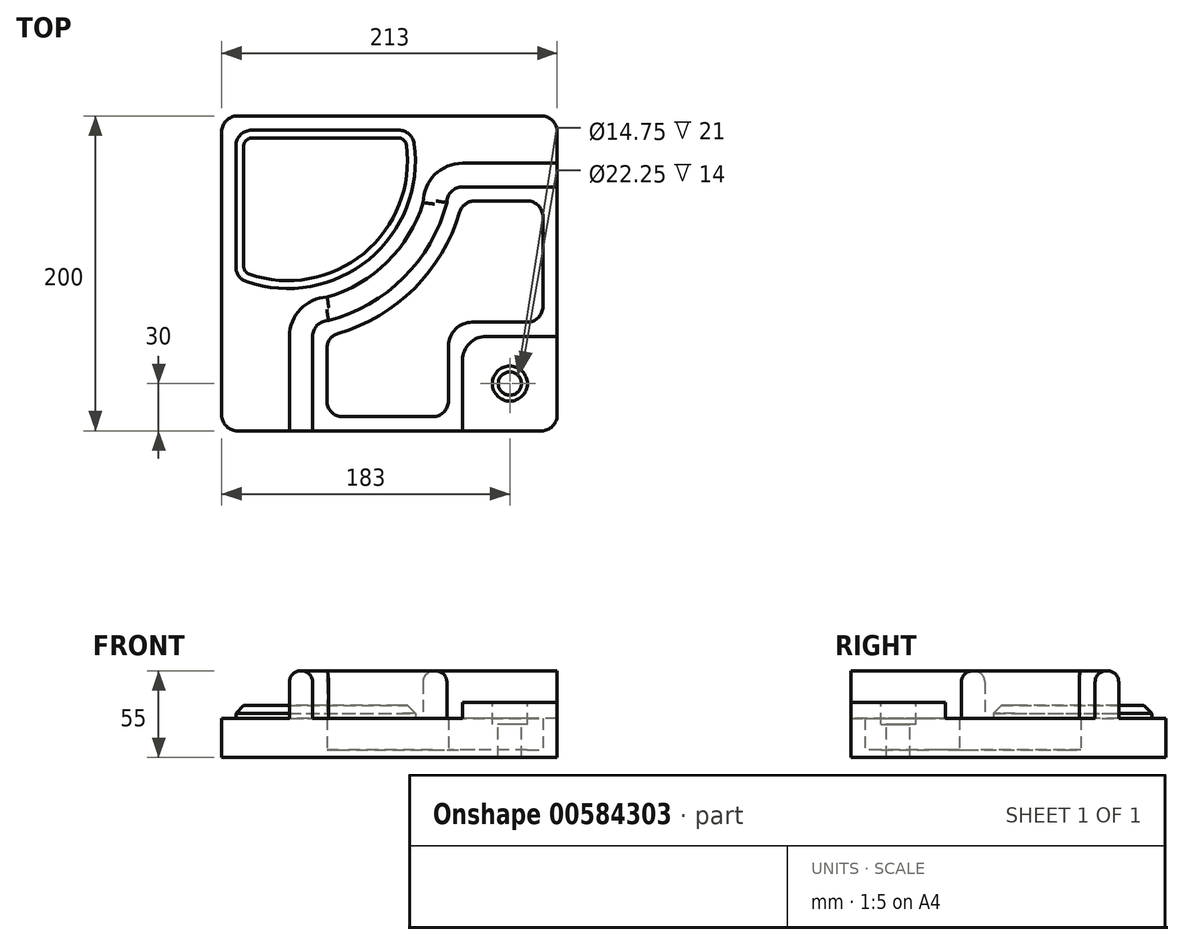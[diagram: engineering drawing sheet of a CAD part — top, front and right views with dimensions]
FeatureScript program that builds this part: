
annotation { "Feature Type Name" : "Feature", "Feature Type Description" : "" }
export const myFeature = defineFeature(function(context is Context, id is Id, definition is map)
    precondition{}
    {
        {
            var Q0;
            Q0=qCreatedBy(makeId("Top.planeOp"),FACE);
            var sketch = newSketch(context, id + "F0", { "sketchPlane" : qUnion([Q0])});
            skLineSegment(sketch, "E0", {"start": v(0, 0) * mm, "end": v(-106.5, 0) * mm});
            skLineSegment(sketch, "E1", {"start": v(-106.5, 0) * mm, "end": v(-106.5, 200) * mm});
            skLineSegment(sketch, "E2.MirrorCS", {"start": v(0, 0) * mm, "end": v(106.5, 0) * mm});
            skLineSegment(sketch, "E3.MirrorCS", {"start": v(106.5, 0) * mm, "end": v(106.5, 200) * mm});
            skLineSegment(sketch, "E4", {"start": v(-106.5, 200) * mm, "end": v(106.5, 200) * mm});
            skLineSegment(sketch, "E5", {"start": v(106.5, 60) * mm, "end": v(46.5, 60) * mm});
            skLineSegment(sketch, "E6", {"start": v(46.5, 60) * mm, "end": v(46.5, 0) * mm});
            skLineSegment(sketch, "E7", {"start": v(-63.5, 0) * mm, "end": v(-63.5, 60) * mm});
            skLineSegment(sketch, "E8", {"start": v(106.5, 170) * mm, "end": v(46.5, 170) * mm});
            skLineSegment(sketch, "E9", {"start": v(-48.73, 0) * mm, "end": v(-48.73, 60) * mm});
            skLineSegment(sketch, "E10", {"start": v(106.5, 155) * mm, "end": v(46.5, 155) * mm});
            skArc(sketch, "E11", {"start": v(-39.51, 84.98) * mm, "mid": v(-56.53, 77.32) * mm, "end": v(-63.5, 60) * mm});
            skArc(sketch, "E12", {"start": v(46.5, 170) * mm, "mid": v(28.82, 162.68) * mm, "end": v(21.5, 145) * mm});
            skArc(sketch, "E13", {"start": v(46.5, 155) * mm, "mid": v(39.43, 152.07) * mm, "end": v(36.5, 145) * mm});
            skArc(sketch, "E14", {"start": v(-38.73, 70) * mm, "mid": v(-45.8, 67.07) * mm, "end": v(-48.73, 60) * mm});
            skArc(sketch, "E15", {"start": v(-39.51, 84.98) * mm, "mid": v(-1.41, 107.27) * mm, "end": v(21.5, 145) * mm});
            skArc(sketch, "E16", {"start": v(-38.73, 70) * mm, "mid": v(9.07, 97.28) * mm, "end": v(36.5, 145) * mm});
            skLineSegment(sketch, "E17", {"start": v(97.5, 146) * mm, "end": v(97.5, 69) * mm});
            skLineSegment(sketch, "E18", {"start": v(97.5, 69) * mm, "end": v(37.5, 69) * mm});
            skLineSegment(sketch, "E19", {"start": v(37.5, 69) * mm, "end": v(37.5, 9) * mm});
            skLineSegment(sketch, "E20", {"start": v(37.5, 9) * mm, "end": v(-39.73, 9) * mm});
            skLineSegment(sketch, "E21", {"start": v(97.5, 146) * mm, "end": v(46.5, 146) * mm});
            skLineSegment(sketch, "E22", {"start": v(-39.73, 9) * mm, "end": v(-39.73, 60) * mm});
            skArc(sketch, "E23", {"start": v(-39.73, 60) * mm, "mid": v(15.83, 90.52) * mm, "end": v(46.5, 146) * mm});
            skArc(sketch, "E24", {"start": v(-97.5, 97.45) * mm, "mid": v(-12.49, 109.37) * mm, "end": v(14.07, 191) * mm});
            skLineSegment(sketch, "E25", {"start": v(0, 0) * mm, "end": v(0, 200) * mm, "construction": true});
            skLineSegment(sketch, "E26", {"start": v(-106.5, 100) * mm, "end": v(106.5, 100) * mm, "construction": true});
            skLineSegment(sketch, "E27", {"start": v(14.07, 191) * mm, "end": v(-97.5, 191) * mm});
            skLineSegment(sketch, "E28", {"start": v(-97.5, 97.45) * mm, "end": v(-97.5, 191) * mm});
            skSolve(sketch);
        }
        {
            var Q0;
            {var subQ1=sQuery(id+"F0.wireOp",EDGE,"E1");Q0=makeQuery(id+"F0.imprint","IMPRINT",FACE,{"disambiguationData":[TD([[makeQuery(id+"F0.imprint","IMPRINT",EDGE,{"derivedFrom":subQ1}),-1.0]])]});}
            var Q1;
            {var subQ6=sQuery(id+"F0.wireOp",EDGE,"E5");Q1=makeQuery(id+"F0.imprint","IMPRINT",FACE,{"disambiguationData":[TD([[makeQuery(id+"F0.imprint","IMPRINT",EDGE,{"derivedFrom":subQ6}),-1.0]])]});}
            extrude(context, id + "F1", {"entities" : qUnion([Q0, Q1]), "depth" : 25 * mm, "offsetDistance" : 25 * mm});
        }
        {
            var Q0;
            Q0=makeQuery(id+"F0.imprint","IMPRINT",FACE,{"disambiguationData":[TD([[makeQuery(id+"F0.imprint","IMPRINT",EDGE,{"derivedFrom":sQuery(id+"F0.wireOp",EDGE,"E24")}),1.0]])]});
            extrude(context, id + "F2", {"entities" : qUnion([Q0]), "operationType" : NewBodyOperationType.ADD, "depth" : 33 * mm, "offsetDistance" : 25 * mm});
        }
        {
            var Q0;
            Q0=makeQuery(id+"F0.imprint","IMPRINT",FACE,{"disambiguationData":[TD([[makeQuery(id+"F0.imprint","IMPRINT",EDGE,{"derivedFrom":sQuery(id+"F0.wireOp",EDGE,"E17")}),-1.0]])]});
            extrude(context, id + "F3", {"entities" : qUnion([Q0]), "operationType" : NewBodyOperationType.ADD, "depth" : 5 * mm, "offsetDistance" : 25 * mm});
        }
        {
            var Q0;
            {var subQ4=sQuery(id+"F0.wireOp",EDGE,"E5");Q0=makeQuery(id+"F0.imprint","IMPRINT",FACE,{"disambiguationData":[TD([[makeQuery(id+"F0.imprint","IMPRINT",EDGE,{"derivedFrom":subQ4}),1.0]])]});}
            extrude(context, id + "F4", {"entities" : qUnion([Q0]), "operationType" : NewBodyOperationType.ADD, "depth" : 35 * mm, "offsetDistance" : 25 * mm});
        }
        {
            var Q0;
            Q0=makeQuery(id+"F4.opExtrude","CAP_FACE",FACE,{"disambiguationData":[OSD([sQuery(id+"F0.wireOp",EDGE,"E2.MirrorCS"),sQuery(id+"F0.wireOp",EDGE,"E3.MirrorCS"),sQuery(id+"F0.wireOp",EDGE,"E5"),sQuery(id+"F0.wireOp",EDGE,"E6")])],"isStart":false});
            var sketch = newSketch(context, id + "F5", { "sketchPlane" : qUnion([Q0])});
            skLineSegment(sketch, "E29", {"start": v(76.5, 60) * mm, "end": v(76.5, 0) * mm, "construction": true});
            skLineSegment(sketch, "E30", {"start": v(46.5, 30) * mm, "end": v(106.5, 30) * mm, "construction": true});
            skPoint(sketch, "E31", {"position": v(76.5, 30) * mm});
            skSolve(sketch);
        }
        {
            var Q0;
            Q0=sQuery(id+"F5.wireOp",VERTEX,"E31");
            var Q1;
            Q1=makeQuery(id+"F1.opExtrude","SWEPT_BODY",BODY,{"disambiguationData":[OSD([sQuery(id+"F0.wireOp",EDGE,"E0"),sQuery(id+"F0.wireOp",EDGE,"E2.MirrorCS"),sQuery(id+"F0.wireOp",EDGE,"E3.MirrorCS"),sQuery(id+"F0.wireOp",EDGE,"E5"),sQuery(id+"F0.wireOp",EDGE,"E6"),sQuery(id+"F0.wireOp",EDGE,"E9"),sQuery(id+"F0.wireOp",EDGE,"E10"),sQuery(id+"F0.wireOp",EDGE,"E13"),sQuery(id+"F0.wireOp",EDGE,"E14"),sQuery(id+"F0.wireOp",EDGE,"E16"),sQuery(id+"F0.wireOp",EDGE,"E17"),sQuery(id+"F0.wireOp",EDGE,"E18"),sQuery(id+"F0.wireOp",EDGE,"E19"),sQuery(id+"F0.wireOp",EDGE,"E20"),sQuery(id+"F0.wireOp",EDGE,"E21"),sQuery(id+"F0.wireOp",EDGE,"E22"),sQuery(id+"F0.wireOp",EDGE,"E23")])]});
            hole(context, id + "F6", {"style" : HoleStyle.C_BORE, "endStyle" : HoleEndStyle.THROUGH, "standardTappedOrClearance" : lookupTablePath({ "standard" : "ISO", "fit" : "Close", "size" : "M14", "type" : "Clearance" }), "standardBlindInLast" : lookupTablePath({ "fit" : "Close", "standard" : "ISO", "size" : "M14", "type" : "Clearance" }), "holeDiameter" : 14.75 * mm, "cBoreDiameter" : 22.25 * mm, "cBoreDepth" : 14 * mm, "majorDiameter" : 5 * mm, "isTappedThrough" : true, "tappedDepth" : 12 * mm, "tapClearance" : 3, "locations" : qUnion([Q0]), "scope" : qUnion([Q1])});
        }
        {
            var Q0;
            {var subQ2=sQuery(id+"F0.wireOp",EDGE,"E7");Q0=makeQuery(id+"F0.imprint","IMPRINT",FACE,{"disambiguationData":[TD([[makeQuery(id+"F0.imprint","IMPRINT",EDGE,{"derivedFrom":subQ2}),-1.0]])]});}
            extrude(context, id + "F7", {"entities" : qUnion([Q0]), "operationType" : NewBodyOperationType.ADD, "depth" : 55 * mm, "offsetDistance" : 25 * mm});
        }
        {
            var Q0;
            Q0=makeQuery(id+"F4.opExtrude","SWEPT_EDGE",EDGE,{"disambiguationData":[OSD([sQuery(id+"F0.wireOp",EDGE,"E2.MirrorCS"),sQuery(id+"F0.wireOp",EDGE,"E3.MirrorCS")])]});
            var Q1;
            Q1=makeQuery(id+"F1.opExtrude","SWEPT_EDGE",EDGE,{"disambiguationData":[OSD([sQuery(id+"F0.wireOp",EDGE,"E0"),sQuery(id+"F0.wireOp",EDGE,"E1")])]});
            var Q2;
            Q2=makeQuery(id+"F1.opExtrude","SWEPT_EDGE",EDGE,{"disambiguationData":[OSD([sQuery(id+"F0.wireOp",EDGE,"E1"),sQuery(id+"F0.wireOp",EDGE,"E4")])]});
            var Q3;
            Q3=makeQuery(id+"F1.opExtrude","SWEPT_EDGE",EDGE,{"disambiguationData":[OSD([sQuery(id+"F0.wireOp",EDGE,"E3.MirrorCS"),sQuery(id+"F0.wireOp",EDGE,"E4")])]});
            fillet(context, id + "F8", {"entities" : qUnion([Q0, Q1, Q2, Q3]), "radius" : 10 * mm, "tangentPropagation" : true, "allowEdgeOverflow" : false});
        }
        {
            var Q0;
            Q0=makeQuery(id+"F1.opExtrude","SWEPT_EDGE",EDGE,{"disambiguationData":[OSD([sQuery(id+"F0.wireOp",EDGE,"E18"),sQuery(id+"F0.wireOp",EDGE,"E19")])]});
            var Q1;
            Q1=makeQuery(id+"F4.opExtrude","SWEPT_EDGE",EDGE,{"disambiguationData":[OSD([sQuery(id+"F0.wireOp",EDGE,"E5"),sQuery(id+"F0.wireOp",EDGE,"E6")])]});
            fillet(context, id + "F9", {"entities" : qUnion([Q0, Q1]), "radius" : 15 * mm, "tangentPropagation" : true, "allowEdgeOverflow" : false});
        }
        {
            var Q0;
            Q0=makeQuery(id+"F1.opExtrude","SWEPT_EDGE",EDGE,{"disambiguationData":[OSD([sQuery(id+"F0.wireOp",EDGE,"E21"),sQuery(id+"F0.wireOp",EDGE,"E23")])]});
            var Q1;
            Q1=makeQuery(id+"F1.opExtrude","SWEPT_EDGE",EDGE,{"disambiguationData":[OSD([sQuery(id+"F0.wireOp",EDGE,"E22"),sQuery(id+"F0.wireOp",EDGE,"E23")])]});
            var Q2;
            Q2=makeQuery(id+"F1.opExtrude","SWEPT_EDGE",EDGE,{"disambiguationData":[OSD([sQuery(id+"F0.wireOp",EDGE,"E17"),sQuery(id+"F0.wireOp",EDGE,"E21")])]});
            var Q3;
            Q3=makeQuery(id+"F1.opExtrude","SWEPT_EDGE",EDGE,{"disambiguationData":[OSD([sQuery(id+"F0.wireOp",EDGE,"E17"),sQuery(id+"F0.wireOp",EDGE,"E18")])]});
            var Q4;
            Q4=makeQuery(id+"F1.opExtrude","SWEPT_EDGE",EDGE,{"disambiguationData":[OSD([sQuery(id+"F0.wireOp",EDGE,"E19"),sQuery(id+"F0.wireOp",EDGE,"E20")])]});
            var Q5;
            Q5=makeQuery(id+"F2.opExtrude","SWEPT_EDGE",EDGE,{"disambiguationData":[OSD([sQuery(id+"F0.wireOp",EDGE,"E24"),sQuery(id+"F0.wireOp",EDGE,"E27")])]});
            var Q6;
            Q6=makeQuery(id+"F2.opExtrude","SWEPT_EDGE",EDGE,{"disambiguationData":[OSD([sQuery(id+"F0.wireOp",EDGE,"E27"),sQuery(id+"F0.wireOp",EDGE,"E28")])]});
            var Q7;
            Q7=makeQuery(id+"F2.opExtrude","SWEPT_EDGE",EDGE,{"disambiguationData":[OSD([sQuery(id+"F0.wireOp",EDGE,"E24"),sQuery(id+"F0.wireOp",EDGE,"E28")])]});
            var Q8;
            Q8=makeQuery(id+"F1.opExtrude","SWEPT_EDGE",EDGE,{"disambiguationData":[OSD([sQuery(id+"F0.wireOp",EDGE,"E20"),sQuery(id+"F0.wireOp",EDGE,"E22")])]});
            fillet(context, id + "F10", {"entities" : qUnion([Q0, Q1, Q2, Q3, Q4, Q5, Q6, Q7, Q8]), "radius" : 10 * mm, "tangentPropagation" : true, "allowEdgeOverflow" : false});
        }
        {
            var Q0;
            Q0=makeQuery(id+"F2.opExtrude","CAP_FACE",FACE,{"disambiguationData":[OSD([sQuery(id+"F0.wireOp",EDGE,"E24"),sQuery(id+"F0.wireOp",EDGE,"E27"),sQuery(id+"F0.wireOp",EDGE,"E28")])],"isStart":false});
            chamfer(context, id + "F11", {"entities" : qUnion([Q0]), "width" : 5 * mm, "tangentPropagation" : true});
        }
        {
            var Q0;
            Q0=makeQuery(id+"F7.opExtrude","CAP_EDGE",EDGE,{"disambiguationData":[OSD([sQuery(id+"F0.wireOp",EDGE,"E9")])],"isStart":false});
            var Q1;
            Q1=makeQuery(id+"F7.opExtrude","CAP_EDGE",EDGE,{"disambiguationData":[OSD([sQuery(id+"F0.wireOp",EDGE,"E7")])],"isStart":false});
            var Q2;
            Q2=makeQuery(id+"F7.opExtrude","CAP_EDGE",EDGE,{"disambiguationData":[OSD([sQuery(id+"F0.wireOp",EDGE,"E11")])],"isStart":false});
            var Q3;
            Q3=makeQuery(id+"F7.opExtrude","CAP_EDGE",EDGE,{"disambiguationData":[OSD([sQuery(id+"F0.wireOp",EDGE,"E15")])],"isStart":false});
            var Q4;
            Q4=makeQuery(id+"F7.opExtrude","CAP_EDGE",EDGE,{"disambiguationData":[OSD([sQuery(id+"F0.wireOp",EDGE,"E16")])],"isStart":false});
            var Q5;
            Q5=makeQuery(id+"F7.opExtrude","CAP_EDGE",EDGE,{"disambiguationData":[OSD([sQuery(id+"F0.wireOp",EDGE,"E13")])],"isStart":false});
            var Q6;
            Q6=makeQuery(id+"F7.opExtrude","CAP_EDGE",EDGE,{"disambiguationData":[OSD([sQuery(id+"F0.wireOp",EDGE,"E12")])],"isStart":false});
            var Q7;
            Q7=makeQuery(id+"F7.opExtrude","CAP_EDGE",EDGE,{"disambiguationData":[OSD([sQuery(id+"F0.wireOp",EDGE,"E14")])],"isStart":false});
            fillet(context, id + "F12", {"entities" : qUnion([Q0, Q1, Q2, Q3, Q4, Q5, Q6, Q7]), "radius" : 7 * mm, "tangentPropagation" : true, "allowEdgeOverflow" : false});
        }
    });
